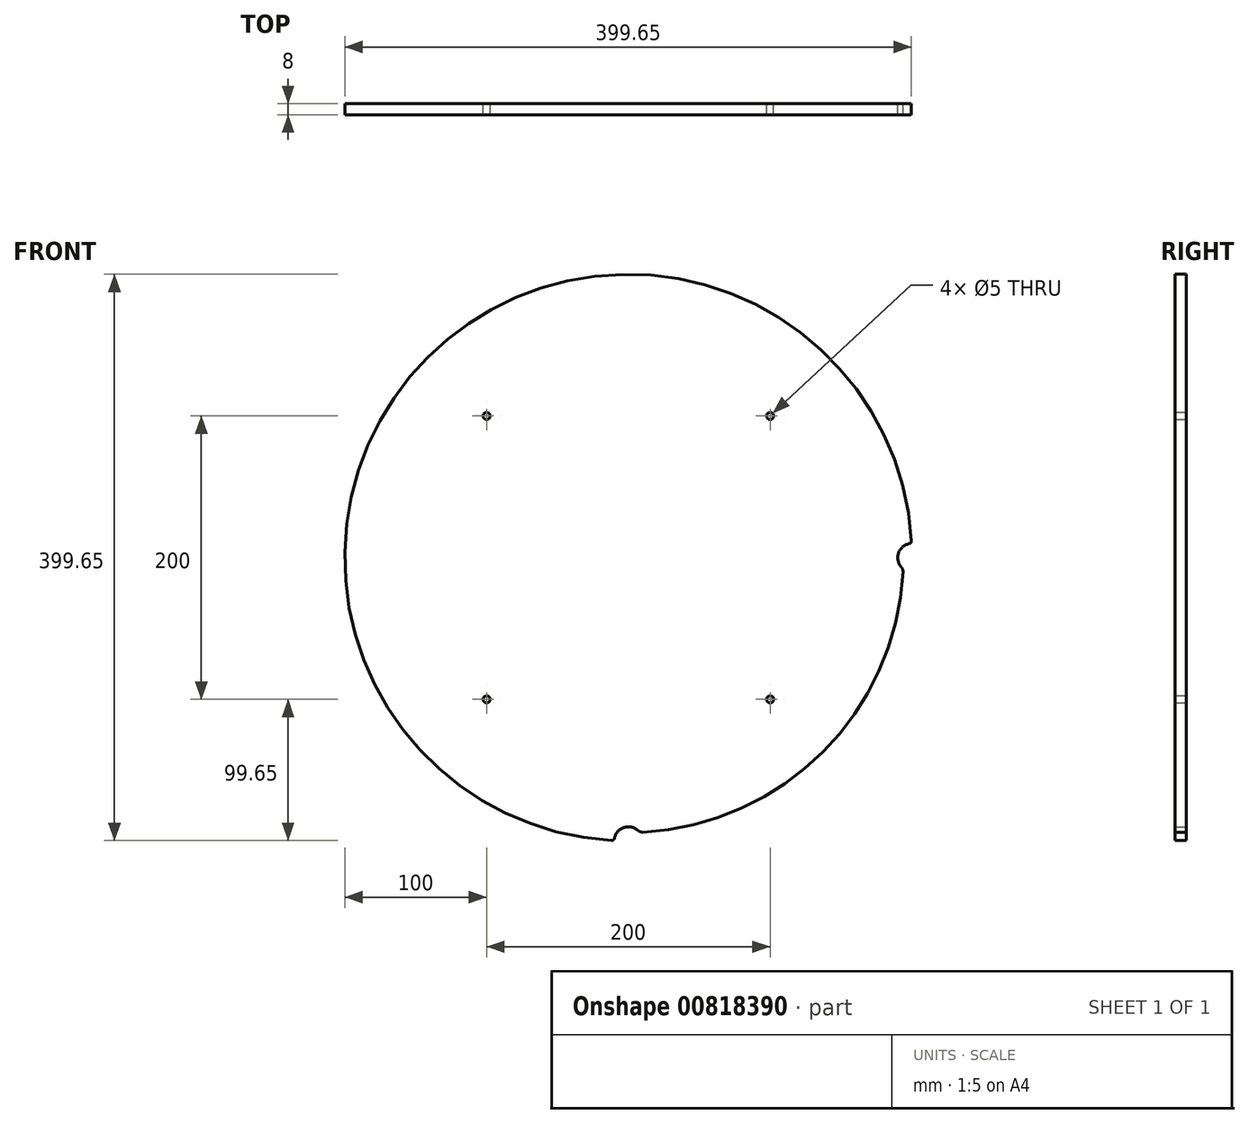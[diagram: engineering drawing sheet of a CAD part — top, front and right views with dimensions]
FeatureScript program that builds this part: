
annotation { "Feature Type Name" : "Feature", "Feature Type Description" : "" }
export const myFeature = defineFeature(function(context is Context, id is Id, definition is map)
    precondition{}
    {
        {
            var Q0;
            Q0=qCreatedBy(makeId("Front.planeOp"),FACE);
            var sketch = newSketch(context, id + "F0", { "sketchPlane" : qUnion([Q0])});
            skArc(sketch, "E0", {"start": v(199.65, 11.89) * mm, "mid": v(-141.42, 141.42) * mm, "end": v(-11.89, -199.65) * mm});
            skLineSegment(sketch, "E1.bottom", {"start": v(100, 100) * mm, "end": v(-100, 100) * mm, "construction": true});
            skLineSegment(sketch, "E1.top", {"start": v(100, -100) * mm, "end": v(-100, -100) * mm, "construction": true});
            skLineSegment(sketch, "E1.left", {"start": v(100, 100) * mm, "end": v(100, -100) * mm, "construction": true});
            skLineSegment(sketch, "E1.right", {"start": v(-100, 100) * mm, "end": v(-100, -100) * mm, "construction": true});
            skCircle(sketch, "E2", {"center": v(-100, 100) * mm, "radius": 2.5 * mm});
            skCircle(sketch, "E3", {"center": v(100, 100) * mm, "radius": 2.5 * mm});
            skCircle(sketch, "E4", {"center": v(100, -100) * mm, "radius": 2.5 * mm});
            skCircle(sketch, "E5", {"center": v(-100, -100) * mm, "radius": 2.5 * mm});
            skArc(sketch, "E6", {"start": v(6.6, -192.5) * mm, "mid": v(-3.2, -190.53) * mm, "end": v(-9.8, -198.04) * mm});
            skArc(sketch, "E7", {"start": v(198.04, 9.8) * mm, "mid": v(190.53, 3.2) * mm, "end": v(192.5, -6.6) * mm});
            skPoint(sketch, "E7.centerSnap0", {"position": v(100, 0) * mm});
            skPoint(sketch, "E8.visualSharp", {"position": v(-10, -199.75) * mm});
            skArc(sketch, "E8.filletArc", {"start": v(-11.89, -199.65) * mm, "mid": v(-10.55, -199.23) * mm, "end": v(-9.8, -198.04) * mm});
            skPoint(sketch, "E9.visualSharp", {"position": v(199.75, 10) * mm});
            skArc(sketch, "E9.filletArc", {"start": v(198.04, 9.8) * mm, "mid": v(199.23, 10.55) * mm, "end": v(199.65, 11.89) * mm});
            skPoint(sketch, "E10.visualSharp", {"position": v(199.75, -10) * mm});
            skPoint(sketch, "E11.visualSharp", {"position": v(10, -199.75) * mm});
            skArc(sketch, "E12", {"start": v(10.17, -193.73) * mm, "mid": v(137.18, -137.18) * mm, "end": v(193.73, -10.17) * mm});
            skArc(sketch, "E13.filletArc", {"start": v(6.6, -192.5) * mm, "mid": v(8.27, -193.46) * mm, "end": v(10.17, -193.73) * mm});
            skArc(sketch, "E14.filletArc", {"start": v(193.73, -10.17) * mm, "mid": v(193.46, -8.27) * mm, "end": v(192.5, -6.6) * mm});
            skSolve(sketch);
        }
        {
            var Q0;
            Q0 = qSketchRegion(id + "F0", true);
            extrude(context, id + "F1", {"entities" : qUnion([Q0]), "depth" : 8 * mm, "offsetDistance" : 25 * mm});
        }
    });
